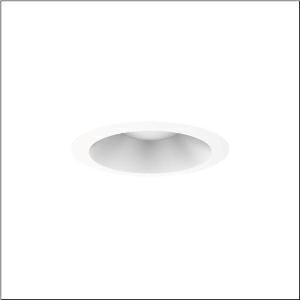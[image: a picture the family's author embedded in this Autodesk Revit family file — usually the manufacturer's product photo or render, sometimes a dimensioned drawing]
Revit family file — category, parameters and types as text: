
# Revit family: lunis_31_midi_51dn167g32
name_source: partatom
category: Lighting Fixtures
units: mm (PartAtom-declared; Revit-internal decimal feet)

## family parameters
Cut with Voids When Loaded = No
Host = Face
Light Source = No
Part Type = Normal
Room Calculation Point = No
Round Connector Dimension = Use Diameter
Shared = No

## types (1)
- Lunis 31 midi (1 x LED, 2000 lm, 17 W, 3000K)
    Apparent Load = 17 VA
    CIE Flux Codes = 64 93 99 100 100
    Color Rendering = 80
    Color Temperature = 3000K
    Default Elevation = 1800 mm
    Description = Lunis 31,  midi, downlight, light control with reflector, light emission: direct distribution, LED rated luminous flux: 2.000lm, light colour: 830, mains connection: 220..240V, AC, 50/60Hz, housing, white, protection rating (complete): IP20, protection rating (on room side): IP54, insulation class (complete): insulation class II (safety insulation), certification: CE, packaging unit: 1 piece
    Height = 0 mm  [stored 0 ft]
    Lamp = 1 x LED
    Lamp Light Flux = 2000 lm
    Lamp Power = 17 W
    Lamp count = 1
    Length = 259 mm
    Luminous efficacy = 118 lm/W
    Manufacturer = Siteco
    ModVariant = No
    Model = 51DN167G32
    Mounting Place = Ceiling
    Mounting Type = Recessed
    Number of Poles = 1
    OnlyDefault = Yes
    Power Factor = 1
    Product Name = Lunis 31 midi
    Product group = downlight
    ProductGroupID = 400
    Protection Class = Protection class II
    Protection Degree = IP 20
    RLX_Detail_Level = 1
    RLX_Emergency_Light_Flux = 0 lm
    RLX_Emergency_Type = 0
    RLX_Emergency_Type_DB = No
    RlxData = <blob elided: 23809 chars, md5=616d82a3>
    Socket = socket
    Standby Power = 0 W
    System Light Flux = 2000 lm
    System Power = 17 W
    Type Comments = Product without accessories
    Type Image = l_1006711.jpg
    URL = http://relux.com
    VarID = ---
    Voltage = 0 V
    Weight = 0.00 kg
    Width = 0 mm  [stored 0 ft]

note: [stored X ft] marks values corroborated as IEEE doubles in the binary element streams (Revit-internal decimal feet)

## geometry (parser evidence)
native form markers: Blend x4, Sweep x12
no freeform markers — native parametric forms only
